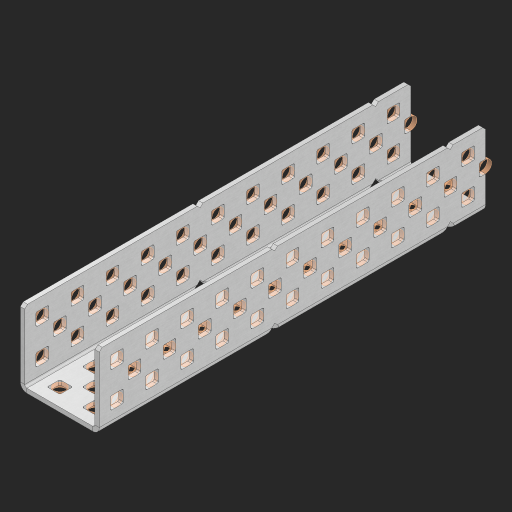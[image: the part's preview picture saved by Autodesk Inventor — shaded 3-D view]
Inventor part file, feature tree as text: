
AUTODESK INVENTOR PART (.ipt)
format: ipt  version: 2023 (Build 270158000, 158)  size: 1,492,992 bytes
history: native  units: in
note: dims shown in document units (in); Inventor stores cm internally (conversion verified against a paired STEP export)
features: other x138, extrude x130, sheet_metal_op x8, sketch x7, mirror x3, pattern_linear x2, chamfer x1
ambient origin geometry x8: Origin, YZ Plane, XZ Plane, XY Plane, X Axis, Y Axis, Z Axis, Center Point
bodies: Solid1 (feature_tree), Body (feature_tree)
feature tree (289):
  sheet_metal_op  "Flanges"
  sheet_metal_op  "Body Pattern"
  pattern_linear  "Center Pattern"  Spacing1=1.0in  [1 undecoded]
  other  "Arc Length"
  mirror  "Notch Mirror"
  pattern_linear  "Notch Pattern"  Spacing1=0.25in  [1 undecoded]
  other  "Diagonal Plane"
  mirror  "Flange 1"
  mirror  "Flange 2"
  chamfer  "End Chamfer"
  sketch  "Sketch1"  dims[d0=1.0in]
  other  "Plate1"
  sketch  "Sketch2"  dims[d1=5.5in]
  other  "Plate2"
  sheet_metal_op  "Bend1"
  sheet_metal_op  "Corner1"
  sketch  "Sketch8"  dims[d2=0.0625in]
  sketch  "Sketch9"  dims[d3=0.0625in]
  other  "Srf91"
  sheet_metal_op  "Body Pattern Sketch"
  other  "Srf92"
  sketch  "Sketch13"  dims[d4=0.0312in]
  sketch  "Sketch15"  dims[d5=0.125in]
  sketch  "Sketch16"  dims[d6=0.0625in d7=1.0in d8=90.0deg d9=0.0312in d10=0.25in d11=0.0625in d12=0.0625in d49=0.182in d50=0.02in d52=0.25in d53=0.0625in d54=0.0in d55=0.172in d56=1.0in d57=0.0in d60=4.3307in d62=0.5in d63=0.7874in d65=0.5in d85=0.1473in d86=0.1782in d88=0.04in d89=0.0625in d90=0.0in d91=0.04in d92=0.0491in d95=2.5in d96=0.04in d97=0.25in d98=45.0deg d99=0.25in d102=2.497in d106=0.182in d107=0.02in d108=0.5in d110=0.0625in d111=0.0in d112=0.172in d113=0.5in d114=0.0in d117=0.5in d118=0.5in d131=0.25in d132=0.25in]
  other  "Srf786"
  other  "Srf889"
  other  "Srf890"
  other  "Srf891"
  other  "Srf892"
  other  "Srf893"
  other  "Srf894"
  other  "Srf895"
  other  "Srf896"
  other  "Srf996"
  other  "Srf997"
  other  "Srf1315"
  other  "Srf1316"
  other  "Srf1317"
  other  "Srf1325"
  other  "Srf1326"
  other  "Srf1327"
  other  "Srf1328"
  other  "Srf1329"
  other  "Srf1330"
  other  "Srf1331"
  other  "Srf1332"
  other  "Srf1338"
  other  "Srf1339"
  other  "Srf1374"
  other  "Srf1375"
  other  "Srf1376"
  other  "Srf1384"
  other  "Srf1385"
  other  "Srf1386"
  other  "Srf1387"
  other  "Srf1388"
  other  "Srf1389"
  other  "Srf1390"
  other  "Srf1391"
  other  "Srf1397"
  other  "Srf1398"
  other  "Srf1433"
  other  "Srf1434"
  other  "Srf1473"
  other  "Srf1474"
  other  "Srf1475"
  other  "Srf1476"
  other  "Srf1477"
  other  "Srf1478"
  other  "Srf1479"
  other  "Srf1480"
  other  "Srf1481"
  other  "Srf1482"
  other  "Srf1483"
  other  "Srf1500"
  other  "Srf1501"
  other  "Srf1502"
  other  "Srf1503"
  other  "Srf1504"
  other  "Srf1505"
  other  "Srf1506"
  other  "Srf1507"
  other  "Srf1508"
  other  "Srf1509"
  other  "Srf1510"
  other  "Srf1511"
  other  "Srf1512"
  other  "Srf1513"
  other  "Srf1514"
  other  "Srf1515"
  other  "Srf1516"
  other  "Srf1517"
  other  "Srf1518"
  other  "Srf1519"
  other  "Srf1538"
  other  "Srf1539"
  other  "Srf1540"
  other  "Srf1541"
  other  "Srf1542"
  other  "Srf1543"
  other  "Srf1544"
  other  "Srf1545"
  other  "Srf1546"
  other  "Srf1547"
  other  "Srf1548"
  other  "Srf1549"
  other  "Srf1550"
  other  "Srf1551"
  other  "Srf1552"
  other  "Srf1553"
  other  "Srf1554"
  other  "Srf1555"
  other  "Srf1556"
  other  "Srf1557"
  other  "Srf1576"
  other  "Srf1577"
  other  "Srf1578"
  other  "Srf1579"
  other  "Srf1580"
  other  "Srf1581"
  other  "Srf1582"
  other  "Srf1583"
  other  "Srf1584"
  other  "Srf1585"
  other  "Srf1586"
  other  "Srf1587"
  other  "Srf1588"
  other  "Srf1589"
  other  "Srf1590"
  other  "Srf1591"
  other  "Srf1592"
  other  "Srf1593"
  other  "Srf1594"
  other  "Srf1595"
  other  "Srf1614"
  other  "Srf1615"
  other  "Srf1616"
  other  "Srf1617"
  other  "Srf1618"
  other  "Srf1619"
  other  "Srf1620"
  other  "Srf1621"
  other  "Srf1622"
  other  "Srf1623"
  other  "Srf1624"
  other  "Srf1625"
  other  "Srf1626"
  other  "Srf1627"
  other  "Srf1628"
  other  "Srf1629"
  other  "Srf1630"
  other  "Srf1631"
  other  "Srf1632"
  other  "Srf1633"
  sheet_metal_op  "Body Stamp"
  sheet_metal_op  "Body Circle"
  other  "Center Stamp"
  other  "Center Circle"
  sheet_metal_op  "Notch"
  extrude  "ExtrusionSrf92"  Depth=0.0625in
  extrude  "ExtrusionSrf889"  Depth=0.0625in
  extrude  "ExtrusionSrf890"  Depth=0.182in
  extrude  "ExtrusionSrf891"  Depth=0.02in
  extrude  "ExtrusionSrf892"  Depth=0.25in
  extrude  "ExtrusionSrf893"  Depth=0.0625in
  extrude  "ExtrusionSrf894"  TaperAngle=0.0deg  [1 undecoded]
  extrude  "ExtrusionSrf895"  Depth=0.25in
  extrude  "ExtrusionSrf896"  Depth=1.0in TaperAngle=0.0deg
  extrude  "ExtrusionSrf996"  Depth=0.25in
  extrude  "ExtrusionSrf997"  Depth=0.5in
  extrude  "ExtrusionSrf1315"  Depth=0.25in
  extrude  "ExtrusionSrf1316"  Depth=0.25in
  extrude  "ExtrusionSrf1355"  Depth=0.25in
  extrude  "ExtrusionSrf1356"  Depth=0.0625in
  extrude  "ExtrusionSrf1357"  TaperAngle=0.0deg  [1 undecoded]
  extrude  "ExtrusionSrf1358"  Depth=0.25in
  extrude  "ExtrusionSrf1359"  Depth=0.25in
  extrude  "ExtrusionSrf1360"  Depth=2.5in
  extrude  "ExtrusionSrf1361"  Depth=0.25in TaperAngle=45.0deg
  extrude  "ExtrusionSrf1362"  Depth=0.25in
  extrude  "ExtrusionSrf1363"  Depth=0.25in
  extrude  "ExtrusionSrf1364"  Depth=0.182in
  extrude  "ExtrusionSrf1365"  Depth=0.02in
  extrude  "ExtrusionSrf1374"  Depth=0.5in
  extrude  "ExtrusionSrf1375"  Depth=0.0625in
  extrude  "ExtrusionSrf1414"  TaperAngle=0.0deg  [1 undecoded]
  extrude  "ExtrusionSrf1415"  Depth=0.25in
  extrude  "ExtrusionSrf1416"  Depth=0.5in TaperAngle=0.0deg
  extrude  "ExtrusionSrf1417"  Depth=0.5in
  extrude  "ExtrusionSrf1418"  Depth=0.5in
  extrude  "ExtrusionSrf1419"  Depth=0.25in
  extrude  "ExtrusionSrf1420"  Depth=0.25in
  extrude  "ExtrusionSrf1421"  [1 undecoded]
  extrude  "ExtrusionSrf1422"  [1 undecoded]
  extrude  "ExtrusionSrf1423"  [1 undecoded]
  extrude  "ExtrusionSrf1424"  [1 undecoded]
  extrude  "ExtrusionSrf1433"  [1 undecoded]
  extrude  "ExtrusionSrf1434"  [1 undecoded]
  extrude  "ExtrusionSrf1473"  [1 undecoded]
  extrude  "ExtrusionSrf1474"  [1 undecoded]
  extrude  "ExtrusionSrf1475"  [1 undecoded]
  extrude  "ExtrusionSrf1476"  [1 undecoded]
  extrude  "ExtrusionSrf1477"  [1 undecoded]
  extrude  "ExtrusionSrf1478"  [1 undecoded]
  extrude  "ExtrusionSrf1479"  [1 undecoded]
  extrude  "ExtrusionSrf1480"  [1 undecoded]
  extrude  "ExtrusionSrf1481"  [1 undecoded]
  extrude  "ExtrusionSrf1482"  [1 undecoded]
  extrude  "ExtrusionSrf1483"  [1 undecoded]
  extrude  "ExtrusionSrf1500"  [1 undecoded]
  extrude  "ExtrusionSrf1501"  [1 undecoded]
  extrude  "ExtrusionSrf1502"  [1 undecoded]
  extrude  "ExtrusionSrf1503"  [1 undecoded]
  extrude  "ExtrusionSrf1504"  [1 undecoded]
  extrude  "ExtrusionSrf1505"  [1 undecoded]
  extrude  "ExtrusionSrf1506"  [1 undecoded]
  extrude  "ExtrusionSrf1507"  [1 undecoded]
  extrude  "ExtrusionSrf1508"  [1 undecoded]
  extrude  "ExtrusionSrf1509"  [1 undecoded]
  extrude  "ExtrusionSrf1510"  [1 undecoded]
  extrude  "ExtrusionSrf1511"  [1 undecoded]
  extrude  "ExtrusionSrf1512"  [1 undecoded]
  extrude  "ExtrusionSrf1513"  [1 undecoded]
  extrude  "ExtrusionSrf1514"  [1 undecoded]
  extrude  "ExtrusionSrf1515"  [1 undecoded]
  extrude  "ExtrusionSrf1516"  [1 undecoded]
  extrude  "ExtrusionSrf1517"  [1 undecoded]
  extrude  "ExtrusionSrf1518"  [1 undecoded]
  extrude  "ExtrusionSrf1519"  [1 undecoded]
  extrude  "ExtrusionSrf1538"  [1 undecoded]
  extrude  "ExtrusionSrf1539"  [1 undecoded]
  extrude  "ExtrusionSrf1540"  [1 undecoded]
  extrude  "ExtrusionSrf1541"  [1 undecoded]
  extrude  "ExtrusionSrf1542"  [1 undecoded]
  extrude  "ExtrusionSrf1543"  [1 undecoded]
  extrude  "ExtrusionSrf1544"  [1 undecoded]
  extrude  "ExtrusionSrf1545"  [1 undecoded]
  extrude  "ExtrusionSrf1546"  [1 undecoded]
  extrude  "ExtrusionSrf1547"  [1 undecoded]
  extrude  "ExtrusionSrf1548"  [1 undecoded]
  extrude  "ExtrusionSrf1549"  [1 undecoded]
  extrude  "ExtrusionSrf1550"  [1 undecoded]
  extrude  "ExtrusionSrf1551"  [1 undecoded]
  extrude  "ExtrusionSrf1552"  [1 undecoded]
  extrude  "ExtrusionSrf1553"  [1 undecoded]
  extrude  "ExtrusionSrf1554"  [1 undecoded]
  extrude  "ExtrusionSrf1555"  [1 undecoded]
  extrude  "ExtrusionSrf1556"  [1 undecoded]
  extrude  "ExtrusionSrf1557"  [1 undecoded]
  extrude  "ExtrusionSrf1576"  [1 undecoded]
  extrude  "ExtrusionSrf1577"  [1 undecoded]
  extrude  "ExtrusionSrf1578"  [1 undecoded]
  extrude  "ExtrusionSrf1579"  [1 undecoded]
  extrude  "ExtrusionSrf1580"  [1 undecoded]
  extrude  "ExtrusionSrf1581"  [1 undecoded]
  extrude  "ExtrusionSrf1582"  [1 undecoded]
  extrude  "ExtrusionSrf1583"  [1 undecoded]
  extrude  "ExtrusionSrf1584"  [1 undecoded]
  extrude  "ExtrusionSrf1585"  [1 undecoded]
  extrude  "ExtrusionSrf1586"  [1 undecoded]
  extrude  "ExtrusionSrf1587"  [1 undecoded]
  extrude  "ExtrusionSrf1588"  [1 undecoded]
  extrude  "ExtrusionSrf1589"  [1 undecoded]
  extrude  "ExtrusionSrf1590"  [1 undecoded]
  extrude  "ExtrusionSrf1591"  [1 undecoded]
  extrude  "ExtrusionSrf1592"  [1 undecoded]
  extrude  "ExtrusionSrf1593"  [1 undecoded]
  extrude  "ExtrusionSrf1594"  [1 undecoded]
  extrude  "ExtrusionSrf1595"  [1 undecoded]
  extrude  "ExtrusionSrf1614"  [1 undecoded]
  extrude  "ExtrusionSrf1615"  [1 undecoded]
  extrude  "ExtrusionSrf1616"  [1 undecoded]
  extrude  "ExtrusionSrf1617"  [1 undecoded]
  extrude  "ExtrusionSrf1618"  [1 undecoded]
  extrude  "ExtrusionSrf1619"  [1 undecoded]
  extrude  "ExtrusionSrf1620"  [1 undecoded]
  extrude  "ExtrusionSrf1621"  [1 undecoded]
  extrude  "ExtrusionSrf1622"  [1 undecoded]
  extrude  "ExtrusionSrf1623"  [1 undecoded]
  extrude  "ExtrusionSrf1624"  [1 undecoded]
  extrude  "ExtrusionSrf1625"  [1 undecoded]
  extrude  "ExtrusionSrf1626"  [1 undecoded]
  extrude  "ExtrusionSrf1627"  [1 undecoded]
  extrude  "ExtrusionSrf1628"  [1 undecoded]
  extrude  "ExtrusionSrf1629"  [1 undecoded]
  extrude  "ExtrusionSrf1630"  [1 undecoded]
  extrude  "ExtrusionSrf1631"  [1 undecoded]
  extrude  "ExtrusionSrf1632"  [1 undecoded]
  extrude  "ExtrusionSrf1633"  [1 undecoded]
note: 102 required parameter values undecoded (feature->parameter linkage not recoverable at this tier; creation-order binding heuristic only, values carry confidence <= 0.55)
